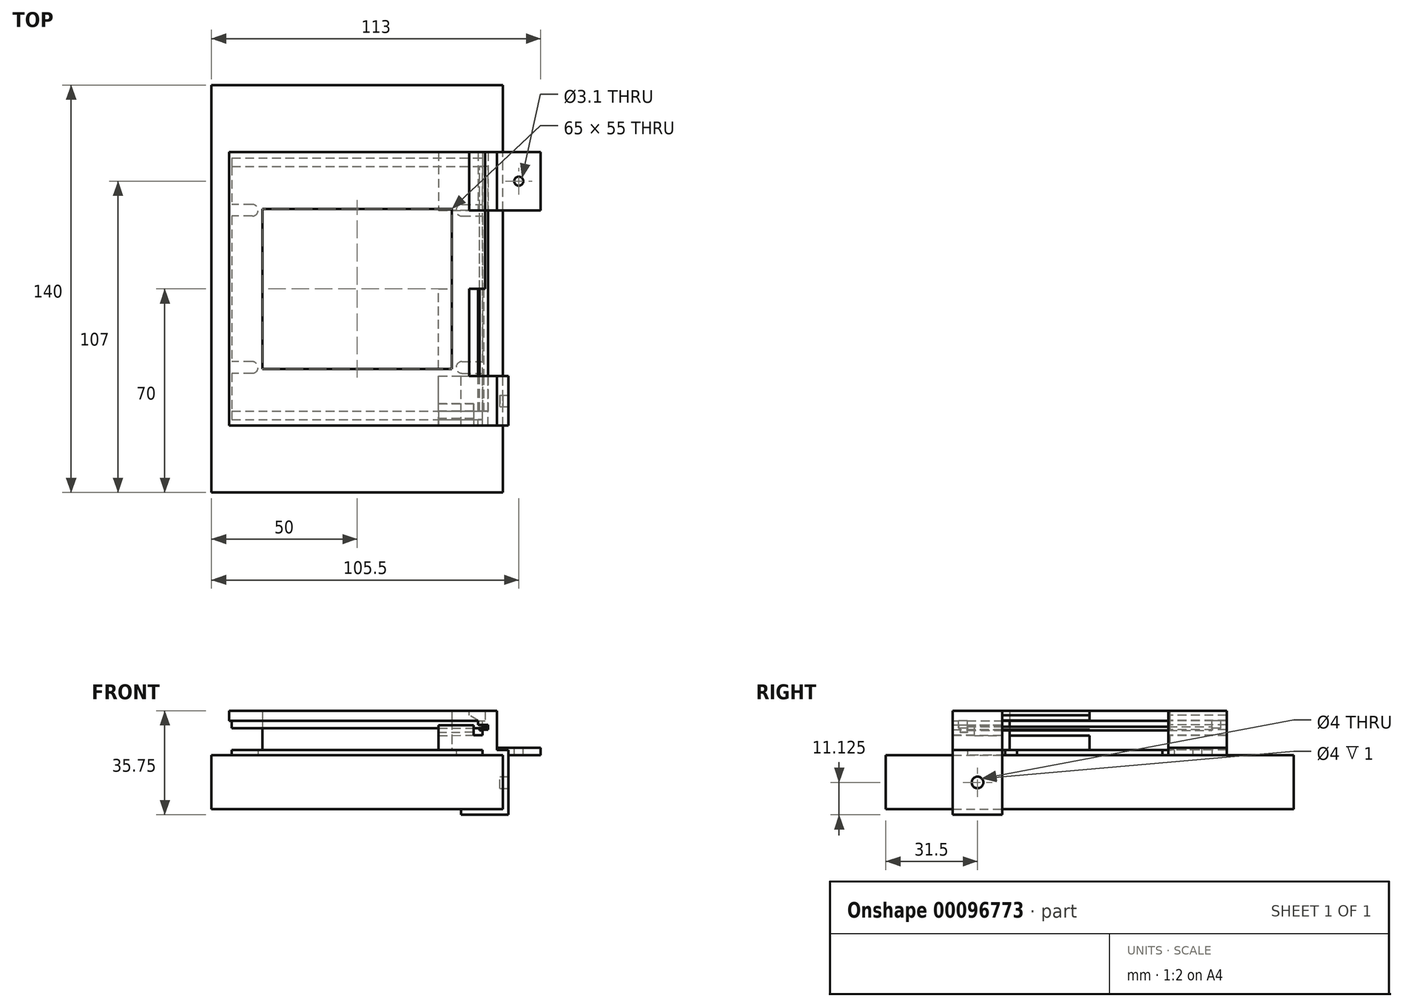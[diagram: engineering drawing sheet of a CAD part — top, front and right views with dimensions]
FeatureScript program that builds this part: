
annotation { "Feature Type Name" : "Feature", "Feature Type Description" : "" }
export const myFeature = defineFeature(function(context is Context, id is Id, definition is map)
    precondition{}
    {
        {
            var Q0;
            Q0=qCreatedBy(makeId("Top.planeOp"),FACE);
            var sketch = newSketch(context, id + "F0", { "sketchPlane" : qUnion([Q0])});
            skLineSegment(sketch, "E0.bottom", {"start": v(-50, -70) * mm, "end": v(50, -70) * mm});
            skLineSegment(sketch, "E0.top", {"start": v(-50, 70) * mm, "end": v(50, 70) * mm});
            skLineSegment(sketch, "E0.left", {"start": v(-50, -70) * mm, "end": v(-50, 70) * mm});
            skLineSegment(sketch, "E0.right", {"start": v(50, -70) * mm, "end": v(50, 70) * mm});
            skPoint(sketch, "E0.middle", {"position": v(0, 0) * mm});
            skSolve(sketch);
        }
        {
            var Q0;
            Q0=qSketchRegion(id+"F0",true);
            extrude(context, id + "F1", {"entities" : qUnion([Q0]), "oppositeDirection" : true, "depth" : 18.5 * mm});
        }
        {
            var Q0;
            Q0=qCreatedBy(makeId("Top.planeOp"),FACE);
            var sketch = newSketch(context, id + "F2", { "sketchPlane" : qUnion([Q0])});
            skLineSegment(sketch, "E1.bottom", {"start": v(-43, 42) * mm, "end": v(43, 42) * mm});
            skLineSegment(sketch, "E1.top", {"start": v(-43, -42) * mm, "end": v(43, -42) * mm});
            skLineSegment(sketch, "E1.left", {"start": v(-43, 42) * mm, "end": v(-43, 29) * mm});
            skLineSegment(sketch, "E1.right", {"start": v(43, 42) * mm, "end": v(43, 29) * mm});
            skPoint(sketch, "E1.middle", {"position": v(0, 0) * mm});
            skArc(sketch, "E2", {"start": v(-36, 25) * mm, "mid": v(-34, 27) * mm, "end": v(-36, 29) * mm});
            skLineSegment(sketch, "E3", {"start": v(-36, 25) * mm, "end": v(-43, 25) * mm});
            skLineSegment(sketch, "E4", {"start": v(-36, 29) * mm, "end": v(-43, 29) * mm});
            skArc(sketch, "E5.MirrorCS", {"start": v(36, 25) * mm, "mid": v(34, 27) * mm, "end": v(36, 29) * mm});
            skLineSegment(sketch, "E6.MirrorCS", {"start": v(36, 29) * mm, "end": v(43, 29) * mm});
            skLineSegment(sketch, "E7.MirrorCS", {"start": v(36, 25) * mm, "end": v(43, 25) * mm});
            skLineSegment(sketch, "E8.MirrorCS", {"start": v(-36, -25) * mm, "end": v(-43, -25) * mm});
            skLineSegment(sketch, "E9.MirrorCS", {"start": v(-36, -29) * mm, "end": v(-43, -29) * mm});
            skArc(sketch, "E10.MirrorCS", {"start": v(-36, -25) * mm, "mid": v(-34, -27) * mm, "end": v(-36, -29) * mm});
            skLineSegment(sketch, "E11.MirrorCS", {"start": v(36, -25) * mm, "end": v(43, -25) * mm});
            skLineSegment(sketch, "E12.MirrorCS", {"start": v(36, -29) * mm, "end": v(43, -29) * mm});
            skArc(sketch, "E13.MirrorCS", {"start": v(36, -25) * mm, "mid": v(34, -27) * mm, "end": v(36, -29) * mm});
            skLineSegment(sketch, "E14.trimOffspring", {"start": v(-43, 25) * mm, "end": v(-43, -25) * mm});
            skLineSegment(sketch, "E15.trimOffspring", {"start": v(-43, -29) * mm, "end": v(-43, -42) * mm});
            skLineSegment(sketch, "E16.trimOffspring", {"start": v(43, -29) * mm, "end": v(43, -42) * mm});
            skLineSegment(sketch, "E17.trimOffspring", {"start": v(43, 25) * mm, "end": v(43, -25) * mm});
            skSolve(sketch);
        }
        {
            var Q0;
            Q0=qSketchRegion(id+"F2",true);
            extrude(context, id + "F3", {"entities" : qUnion([Q0]), "depth" : 1.75 * mm});
        }
        {
            var Q0;
            Q0=makeQuery(id+"F3.opExtrude","CAP_FACE",FACE,{"disambiguationData":[OSD([sQuery(id+"F2.wireOp",EDGE,"E1.bottom"),sQuery(id+"F2.wireOp",EDGE,"E1.top"),sQuery(id+"F2.wireOp",EDGE,"E1.left"),sQuery(id+"F2.wireOp",EDGE,"E1.right"),sQuery(id+"F2.wireOp",EDGE,"E2"),sQuery(id+"F2.wireOp",EDGE,"E3"),sQuery(id+"F2.wireOp",EDGE,"E4"),sQuery(id+"F2.wireOp",EDGE,"E5.MirrorCS"),sQuery(id+"F2.wireOp",EDGE,"E6.MirrorCS"),sQuery(id+"F2.wireOp",EDGE,"E7.MirrorCS"),sQuery(id+"F2.wireOp",EDGE,"E8.MirrorCS"),sQuery(id+"F2.wireOp",EDGE,"E9.MirrorCS"),sQuery(id+"F2.wireOp",EDGE,"E10.MirrorCS"),sQuery(id+"F2.wireOp",EDGE,"E11.MirrorCS"),sQuery(id+"F2.wireOp",EDGE,"E12.MirrorCS"),sQuery(id+"F2.wireOp",EDGE,"E13.MirrorCS"),sQuery(id+"F2.wireOp",EDGE,"E14.trimOffspring"),sQuery(id+"F2.wireOp",EDGE,"E15.trimOffspring"),sQuery(id+"F2.wireOp",EDGE,"E16.trimOffspring"),sQuery(id+"F2.wireOp",EDGE,"E17.trimOffspring")])],"isStart":false});
            var sketch = newSketch(context, id + "F4", { "sketchPlane" : qUnion([Q0])});
            skLineSegment(sketch, "E18.bottom", {"start": v(-45, 47) * mm, "end": v(45, 47) * mm});
            skLineSegment(sketch, "E18.top", {"start": v(-45, -47) * mm, "end": v(45, -47) * mm});
            skLineSegment(sketch, "E18.left", {"start": v(-45, 47) * mm, "end": v(-45, -47) * mm});
            skLineSegment(sketch, "E18.right", {"start": v(45, 47) * mm, "end": v(45, -47) * mm});
            skPoint(sketch, "E18.middle", {"position": v(0, 0) * mm});
            skLineSegment(sketch, "E19.bottom", {"start": v(-43, 45) * mm, "end": v(43, 45) * mm});
            skLineSegment(sketch, "E19.top", {"start": v(-43, -45) * mm, "end": v(43, -45) * mm});
            skLineSegment(sketch, "E19.left", {"start": v(-43, 45) * mm, "end": v(-43, -45) * mm});
            skLineSegment(sketch, "E19.right", {"start": v(43, 45) * mm, "end": v(43, -45) * mm});
            skLineSegment(sketch, "E20", {"start": v(-43, 45) * mm, "end": v(-45, 45) * mm});
            skLineSegment(sketch, "E21", {"start": v(43, 45) * mm, "end": v(45, 45) * mm});
            skLineSegment(sketch, "E22.MirrorCS", {"start": v(-43, -45) * mm, "end": v(-45, -45) * mm});
            skLineSegment(sketch, "E23.MirrorCS", {"start": v(43, -45) * mm, "end": v(45, -45) * mm});
            skLineSegment(sketch, "E24", {"start": v(-43, 45) * mm, "end": v(-43, 47) * mm});
            skLineSegment(sketch, "E25.MirrorCS", {"start": v(43, 45) * mm, "end": v(43, 47) * mm});
            skLineSegment(sketch, "E26.MirrorCS", {"start": v(-43, -45) * mm, "end": v(-43, -47) * mm});
            skLineSegment(sketch, "E27.MirrorCS", {"start": v(43, -45) * mm, "end": v(43, -47) * mm});
            skLineSegment(sketch, "E28.bottom", {"start": v(-32.5, 27.5) * mm, "end": v(32.5, 27.5) * mm});
            skLineSegment(sketch, "E28.top", {"start": v(-32.5, -27.5) * mm, "end": v(32.5, -27.5) * mm});
            skLineSegment(sketch, "E28.left", {"start": v(-32.5, 27.5) * mm, "end": v(-32.5, -27.5) * mm});
            skLineSegment(sketch, "E28.right", {"start": v(32.5, 27.5) * mm, "end": v(32.5, -27.5) * mm});
            skSolve(sketch);
        }
        {
            var Q0;
            Q0=makeQuery(id+"F4.imprint","IMPRINT",FACE,{"disambiguationData":[TD([[makeQuery(id+"F4.imprint","IMPRINT",EDGE,{"derivedFrom":sQuery(id+"F4.wireOp",EDGE,"E28.bottom")}),-1.0]])]});
            extrude(context, id + "F5", {"entities" : qUnion([Q0]), "depth" : 10 * mm});
        }
        {
            var Q0;
            Q0=makeQuery(id+"F5.opExtrude","CAP_FACE",FACE,{"disambiguationData":[OSD([sQuery(id+"F4.wireOp",EDGE,"E28.bottom"),sQuery(id+"F4.wireOp",EDGE,"E28.top"),sQuery(id+"F4.wireOp",EDGE,"E28.left"),sQuery(id+"F4.wireOp",EDGE,"E28.right")])],"isStart":false});
            var sketch = newSketch(context, id + "F6", { "sketchPlane" : qUnion([Q0])});
            skLineSegment(sketch, "E29.bottom", {"start": v(-44, 47) * mm, "end": v(44, 47) * mm});
            skLineSegment(sketch, "E29.top", {"start": v(-44, -47) * mm, "end": v(44, -47) * mm});
            skLineSegment(sketch, "E29.left", {"start": v(-44, 47) * mm, "end": v(-44, -47) * mm});
            skLineSegment(sketch, "E29.right", {"start": v(44, 47) * mm, "end": v(44, -47) * mm});
            skPoint(sketch, "E29.middle", {"position": v(0, 0) * mm});
            skLineSegment(sketch, "E30.bottom", {"start": v(-43, 45) * mm, "end": v(43, 45) * mm});
            skLineSegment(sketch, "E30.top", {"start": v(-43, -45) * mm, "end": v(43, -45) * mm});
            skLineSegment(sketch, "E30.left", {"start": v(-43, 45) * mm, "end": v(-43, -45) * mm});
            skLineSegment(sketch, "E30.right", {"start": v(43, 45) * mm, "end": v(43, -45) * mm});
            skLineSegment(sketch, "E31.MirrorCS", {"start": v(-43, -44) * mm, "end": v(-43, -45) * mm});
            skLineSegment(sketch, "E32.MirrorCS", {"start": v(43, -44) * mm, "end": v(43, -45) * mm});
            skLineSegment(sketch, "E33.bottom", {"start": v(-32.5, 27.5) * mm, "end": v(32.5, 27.5) * mm});
            skLineSegment(sketch, "E33.top", {"start": v(-32.5, -27.5) * mm, "end": v(32.5, -27.5) * mm});
            skLineSegment(sketch, "E33.left", {"start": v(-32.5, 27.5) * mm, "end": v(-32.5, -27.5) * mm});
            skLineSegment(sketch, "E33.right", {"start": v(32.5, 27.5) * mm, "end": v(32.5, -27.5) * mm});
            skLineSegment(sketch, "E34.0", {"start": v(-43, 42) * mm, "end": v(43, 42) * mm});
            skLineSegment(sketch, "E35.0", {"start": v(-43, -42) * mm, "end": v(43, -42) * mm});
            skSolve(sketch);
        }
        {
            var Q0;
            Q0=makeQuery(id+"F6.imprint","IMPRINT",FACE,{"disambiguationData":[TD([[makeQuery(id+"F6.imprint","IMPRINT",EDGE,{"derivedFrom":sQuery(id+"F6.wireOp",EDGE,"E30.bottom")}),1.0]])]});
            var Q1;
            {var subQ0=sQuery(id+"F6.wireOp",EDGE,"E30.bottom");Q1=makeQuery(id+"F6.imprint","IMPRINT",FACE,{"disambiguationData":[TD([[makeQuery(id+"F6.imprint","IMPRINT",EDGE,{"derivedFrom":subQ0}),-1.0]])]});}
            var Q2;
            Q2=makeQuery(id+"F6.imprint","IMPRINT",FACE,{"disambiguationData":[TD([[makeQuery(id+"F6.imprint","IMPRINT",EDGE,{"derivedFrom":sQuery(id+"F6.wireOp",EDGE,"E33.bottom")}),1.0]])]});
            var Q3;
            {var subQ0=sQuery(id+"F6.wireOp",EDGE,"E30.top");Q3=makeQuery(id+"F6.imprint","IMPRINT",FACE,{"disambiguationData":[TD([[makeQuery(id+"F6.imprint","IMPRINT",EDGE,{"derivedFrom":subQ0}),1.0]])]});}
            var Q4;
            Q4=makeQuery(id+"F6.imprint","IMPRINT",FACE,{"disambiguationData":[TD([[makeQuery(id+"F6.imprint","IMPRINT",EDGE,{"derivedFrom":sQuery(id+"F6.wireOp",EDGE,"E30.top")}),-1.0]])]});
            extrude(context, id + "F7", {"entities" : qUnion([Q0, Q1, Q2, Q3, Q4]), "depth" : 3.5 * mm});
        }
        {
            var Q0;
            {var subQ0=sQuery(id+"F6.wireOp",EDGE,"E30.bottom");Q0=makeQuery(id+"F6.imprint","IMPRINT",FACE,{"disambiguationData":[TD([[makeQuery(id+"F6.imprint","IMPRINT",EDGE,{"derivedFrom":subQ0}),-1.0]])]});}
            var Q1;
            {var subQ0=sQuery(id+"F6.wireOp",EDGE,"E30.top");Q1=makeQuery(id+"F6.imprint","IMPRINT",FACE,{"disambiguationData":[TD([[makeQuery(id+"F6.imprint","IMPRINT",EDGE,{"derivedFrom":subQ0}),1.0]])]});}
            extrude(context, id + "F8", {"entities" : qUnion([Q0, Q1]), "operationType" : NewBodyOperationType.ADD, "oppositeDirection" : true, "depth" : 2.5 * mm});
        }
        {
            var Q0;
            Q0=qCreatedBy(makeId("Front.planeOp"),FACE);
            var sketch = newSketch(context, id + "F9", { "sketchPlane" : qUnion([Q0])});
            skLineSegment(sketch, "E36.0", {"start": v(43, 13.75) * mm, "end": v(43, 10.25) * mm});
            skLineSegment(sketch, "E37.0", {"start": v(43, 13.75) * mm, "end": v(43, 9.75) * mm});
            skLineSegment(sketch, "E38.0", {"start": v(43, 7.25) * mm, "end": v(43, 9.75) * mm});
            skLineSegment(sketch, "E39", {"start": v(43, 9.75) * mm, "end": v(43, 8.5) * mm});
            skLineSegment(sketch, "E40", {"start": v(43, 8.5) * mm, "end": v(45, 9.75) * mm});
            skLineSegment(sketch, "E41", {"start": v(45, 9.75) * mm, "end": v(43, 9.75) * mm});
            skLineSegment(sketch, "E42.bottom", {"start": v(43, 9.75) * mm, "end": v(42, 9.75) * mm});
            skLineSegment(sketch, "E42.top", {"start": v(43, 8.5) * mm, "end": v(42, 8.5) * mm});
            skLineSegment(sketch, "E42.right", {"start": v(42, 9.75) * mm, "end": v(42, 8.5) * mm});
            skSolve(sketch);
        }
        {
            var Q0;
            Q0=qSketchRegion(id+"F9",true);
            extrude(context, id + "F10", {"entities" : qUnion([Q0]), "operationType" : NewBodyOperationType.ADD, "depth" : 42 * mm, "hasSecondDirection" : true, "secondDirectionOppositeDirection" : true, "secondDirectionDepth" : 42 * mm});
        }
        {
            var Q0;
            Q0=qCreatedBy(makeId("Front.planeOp"),FACE);
            var sketch = newSketch(context, id + "F11", { "sketchPlane" : qUnion([Q0])});
            skLineSegment(sketch, "E43.0", {"start": v(28, 1.75) * mm, "end": v(43, 1.75) * mm});
            skLineSegment(sketch, "E44.0", {"start": v(43, 1.75) * mm, "end": v(43, 0) * mm});
            skLineSegment(sketch, "E45", {"start": v(43, 0) * mm, "end": v(48, 0) * mm});
            skPoint(sketch, "E46.orphan", {"position": v(43, 9.75) * mm});
            skPoint(sketch, "E47.orphan", {"position": v(-43, 9.25) * mm});
            skPoint(sketch, "E48.orphan", {"position": v(-43, 1.75) * mm});
            skPoint(sketch, "E49.end.orphan", {"position": v(43, 7.25) * mm});
            skLineSegment(sketch, "E50", {"start": v(27.97, 6.75) * mm, "end": v(28, 1.75) * mm});
            skLineSegment(sketch, "E51", {"start": v(48, 13.75) * mm, "end": v(48, 1.75) * mm});
            skPoint(sketch, "E52.0.end.orphan", {"position": v(45, 9.75) * mm});
            skLineSegment(sketch, "E53.0", {"start": v(45, 9.75) * mm, "end": v(43, 9.75) * mm, "construction": true});
            skLineSegment(sketch, "E54.0", {"start": v(43, 8.5) * mm, "end": v(45, 9.75) * mm, "construction": true});
            skLineSegment(sketch, "E55", {"start": v(27.97, 6.75) * mm, "end": v(43, 6.84) * mm});
            skLineSegment(sketch, "E56.bottom", {"start": v(43, 0) * mm, "end": v(52, 0) * mm});
            skLineSegment(sketch, "E56.top", {"start": v(48, 1.75) * mm, "end": v(52, 1.75) * mm});
            skLineSegment(sketch, "E56.left", {"start": v(43, 0) * mm, "end": v(43, 1.75) * mm});
            skLineSegment(sketch, "E57.right", {"start": v(41.5, 11.88) * mm, "end": v(41.5, 10.45) * mm});
            skLineSegment(sketch, "E58", {"start": v(38.5, 13.75) * mm, "end": v(41.5, 11.88) * mm});
            skLineSegment(sketch, "E59", {"start": v(41.5, 10.45) * mm, "end": v(44.97, 10.45) * mm});
            skLineSegment(sketch, "E60", {"start": v(44.97, 10.45) * mm, "end": v(45, 8.79) * mm});
            skLineSegment(sketch, "E61", {"start": v(45, 8.79) * mm, "end": v(43, 8.75) * mm});
            skPoint(sketch, "E62.orphan", {"position": v(43, 10) * mm});
            skPoint(sketch, "E63.orphan", {"position": v(41.5, 10) * mm});
            skLineSegment(sketch, "E64", {"start": v(43, 8.75) * mm, "end": v(43, 6.84) * mm});
            skLineSegment(sketch, "E65.top", {"start": v(38.5, 15.25) * mm, "end": v(48, 15.25) * mm});
            skLineSegment(sketch, "E65.left", {"start": v(38.5, 13.75) * mm, "end": v(38.5, 15.25) * mm});
            skLineSegment(sketch, "E65.right", {"start": v(48, 13.75) * mm, "end": v(48, 15.25) * mm});
            skPoint(sketch, "E57.bottom.end.orphan", {"position": v(41.5, 13.75) * mm});
            skLineSegment(sketch, "E66.0", {"start": v(50, -18.5) * mm, "end": v(50, 0) * mm});
            skLineSegment(sketch, "E67.0", {"start": v(-50, -18.5) * mm, "end": v(50, -18.5) * mm});
            skLineSegment(sketch, "E68", {"start": v(48, 0) * mm, "end": v(50, 0) * mm});
            skLineSegment(sketch, "E69", {"start": v(50, -18.5) * mm, "end": v(35.7, -18.5) * mm});
            skLineSegment(sketch, "E70", {"start": v(35.7, -18.5) * mm, "end": v(35.7, -20.5) * mm});
            skLineSegment(sketch, "E71", {"start": v(35.7, -20.5) * mm, "end": v(52, -20.5) * mm});
            skLineSegment(sketch, "E72", {"start": v(52, -20.5) * mm, "end": v(52, 1.75) * mm});
            skPoint(sketch, "E56.right.end.orphan", {"position": v(63, 1.75) * mm});
            skSolve(sketch);
        }
        {
            var Q0;
            Q0=qSketchRegion(id+"F11",true);
            extrude(context, id + "F12", {"entities" : qUnion([Q0]), "depth" : 47 * mm});
        }
        {
            var Q0;
            Q0=qSketchRegion(id+"F11",true);
            extrude(context, id + "F13", {"entities" : qUnion([Q0]), "operationType" : NewBodyOperationType.REMOVE, "depth" : 30 * mm});
        }
        {
            var Q0;
            Q0=makeQuery(id+"F12.opExtrude","SWEPT_FACE",FACE,{"disambiguationData":[OSD([sQuery(id+"F11.wireOp",EDGE,"E50")])]});
            var sketch = newSketch(context, id + "F14", { "sketchPlane" : qUnion([Q0])});
            skPoint(sketch, "E73.right.end.orphan", {"position": v(-45, -81.5) * mm});
            skPoint(sketch, "E74.0.end.orphan", {"position": v(42, 12) * mm});
            skPoint(sketch, "E74.0.start.orphan", {"position": v(-42, 9.5) * mm});
            skPoint(sketch, "E75.0.end.orphan", {"position": v(-45, 12) * mm});
            skPoint(sketch, "E75.0.start.orphan", {"position": v(-45, 9.5) * mm});
            skPoint(sketch, "E76.0.end.orphan", {"position": v(-45, 9.08) * mm});
            skPoint(sketch, "E76.0.start.orphan", {"position": v(42, 7.08) * mm});
            skPoint(sketch, "E77.0.3.end.orphan", {"position": v(47, 6.58) * mm});
            skPoint(sketch, "E77.0.3.start.orphan", {"position": v(47, 6.58) * mm});
            skPoint(sketch, "E77.0.1.end.orphan", {"position": v(30, 6.58) * mm});
            skPoint(sketch, "E77.0.1.start.orphan", {"position": v(30, 6.58) * mm});
            skLineSegment(sketch, "E78.0", {"start": v(-45, 9.5) * mm, "end": v(-45, 12) * mm, "construction": true});
            skLineSegment(sketch, "E79.0", {"start": v(42, 8.25) * mm, "end": v(42, 9.58) * mm, "construction": true});
            skLineSegment(sketch, "E80.0", {"start": v(-45, 12) * mm, "end": v(-46, 12) * mm, "construction": true});
            skLineSegment(sketch, "E81.0", {"start": v(-45, 12) * mm, "end": v(-135, 12) * mm, "construction": true});
            skLineSegment(sketch, "E82.top", {"start": v(47, 5.94) * mm, "end": v(39.5, 5.94) * mm});
            skPoint(sketch, "E83.orphan", {"position": v(39.5, 7.08) * mm});
            skLineSegment(sketch, "E84", {"start": v(-45, 11.58) * mm, "end": v(-45, 9.08) * mm});
            skLineSegment(sketch, "E85", {"start": v(47, 10.08) * mm, "end": v(47, 5.94) * mm});
            skPoint(sketch, "E86.orphan", {"position": v(-42, 8.25) * mm});
            skLineSegment(sketch, "E87.right", {"start": v(47, 10.08) * mm, "end": v(47, 7.08) * mm});
            skPoint(sketch, "E88.orphan", {"position": v(45, 12) * mm});
            skPoint(sketch, "E89.0.start.orphan", {"position": v(45, 9.5) * mm});
            skLineSegment(sketch, "E90", {"start": v(44.5, 10.08) * mm, "end": v(44.5, 7.58) * mm});
            skLineSegment(sketch, "E91", {"start": v(42, 7.58) * mm, "end": v(42, 9.58) * mm});
            skLineSegment(sketch, "E92", {"start": v(39.5, 9.58) * mm, "end": v(39.5, 5.94) * mm});
            skLineSegment(sketch, "E93", {"start": v(42, 7.58) * mm, "end": v(44.5, 7.58) * mm});
            skLineSegment(sketch, "E94.top", {"start": v(42, 10.08) * mm, "end": v(39.5, 10.08) * mm});
            skLineSegment(sketch, "E94.left", {"start": v(42, 9.58) * mm, "end": v(42, 10.08) * mm});
            skLineSegment(sketch, "E94.right", {"start": v(39.5, 9.58) * mm, "end": v(39.5, 10.08) * mm});
            skLineSegment(sketch, "E95", {"start": v(44.5, 10.08) * mm, "end": v(47, 10.08) * mm});
            skSolve(sketch);
        }
        {
            var Q0;
            Q0=qSketchRegion(id+"F14",true);
            extrude(context, id + "F15", {"entities" : qUnion([Q0]), "operationType" : NewBodyOperationType.ADD, "oppositeDirection" : true, "depth" : 12 * mm});
        }
        {
            var Q0;
            Q0=makeQuery(id+"F12.opExtrude","SWEPT_FACE",FACE,{"disambiguationData":[OSD([sQuery(id+"F11.wireOp",EDGE,"E72")])]});
            var sketch = newSketch(context, id + "F16", { "sketchPlane" : qUnion([Q0])});
            skCircle(sketch, "E96", {"center": v(-38.5, -9.38) * mm, "radius": 2 * mm});
            skPoint(sketch, "E96.centerSnap0", {"position": v(-47, -9.38) * mm});
            skPoint(sketch, "E96.centerSnap1", {"position": v(-38.5, 1.75) * mm});
            skSolve(sketch);
        }
        {
            var Q0;
            Q0=qSketchRegion(id+"F16",true);
            extrude(context, id + "F17", {"entities" : qUnion([Q0]), "operationType" : NewBodyOperationType.REMOVE, "oppositeDirection" : true, "depth" : 3 * mm});
        }
        {
            var Q0;
            Q0=makeQuery(id+"F13.boolean.opBoolean","COPY",FACE,{"derivedFrom":makeQuery(id+"F13.opExtrude","CAP_FACE",FACE,{"disambiguationData":[OSD([sQuery(id+"F11.wireOp",EDGE,"E43.0"),sQuery(id+"F11.wireOp",EDGE,"E50"),sQuery(id+"F11.wireOp",EDGE,"E51"),sQuery(id+"F11.wireOp",EDGE,"E55"),sQuery(id+"F11.wireOp",EDGE,"E56.bottom"),sQuery(id+"F11.wireOp",EDGE,"E56.top"),sQuery(id+"F11.wireOp",EDGE,"E56.left"),sQuery(id+"F11.wireOp",EDGE,"E57.right"),sQuery(id+"F11.wireOp",EDGE,"E58"),sQuery(id+"F11.wireOp",EDGE,"E59"),sQuery(id+"F11.wireOp",EDGE,"E60"),sQuery(id+"F11.wireOp",EDGE,"E61"),sQuery(id+"F11.wireOp",EDGE,"E64"),sQuery(id+"F11.wireOp",EDGE,"E65.top"),sQuery(id+"F11.wireOp",EDGE,"E65.left"),sQuery(id+"F11.wireOp",EDGE,"E65.right"),sQuery(id+"F11.wireOp",EDGE,"E66.0"),sQuery(id+"F11.wireOp",EDGE,"E68"),sQuery(id+"F11.wireOp",EDGE,"E69"),sQuery(id+"F11.wireOp",EDGE,"E70"),sQuery(id+"F11.wireOp",EDGE,"E71"),sQuery(id+"F11.wireOp",EDGE,"E72")])],"isStart":false})});
            cPlane(context, id + "F18", {"entities" : qUnion([Q0]), "cplaneType" : CPlaneType.OFFSET, "offset" : 57 * mm, "width" : 150 * mm, "height" : 150 * mm});
        }
        {
            var Q0;
            Q0=qCreatedBy(id+"F18.planeOp",FACE);
            var sketch = newSketch(context, id + "F19", { "sketchPlane" : qUnion([Q0])});
            skLineSegment(sketch, "E97.0.0", {"start": v(-28, 1.75) * mm, "end": v(-27.97, 6.75) * mm});
            skLineSegment(sketch, "E97.0.1", {"start": v(-27.97, 6.75) * mm, "end": v(-43, 6.84) * mm});
            skLineSegment(sketch, "E97.0.2", {"start": v(-43, 6.84) * mm, "end": v(-43, 8.75) * mm});
            skLineSegment(sketch, "E97.0.3", {"start": v(-43, 8.75) * mm, "end": v(-45, 8.79) * mm});
            skLineSegment(sketch, "E97.0.4", {"start": v(-45, 8.79) * mm, "end": v(-44.97, 10.45) * mm});
            skLineSegment(sketch, "E97.0.5", {"start": v(-44.97, 10.45) * mm, "end": v(-41.5, 10.45) * mm});
            skLineSegment(sketch, "E97.0.6", {"start": v(-41.5, 10.45) * mm, "end": v(-41.5, 11.88) * mm});
            skLineSegment(sketch, "E97.0.7", {"start": v(-41.5, 11.88) * mm, "end": v(-38.5, 13.75) * mm});
            skLineSegment(sketch, "E97.0.8", {"start": v(-38.5, 13.75) * mm, "end": v(-38.5, 15.25) * mm});
            skLineSegment(sketch, "E97.0.9", {"start": v(-38.5, 15.25) * mm, "end": v(-48, 15.25) * mm});
            skLineSegment(sketch, "E97.0.10", {"start": v(-48, 15.25) * mm, "end": v(-48, 2.5) * mm});
            skLineSegment(sketch, "E97.0.18", {"start": v(-43, 0) * mm, "end": v(-43, 1.75) * mm});
            skLineSegment(sketch, "E97.0.19", {"start": v(-43, 1.75) * mm, "end": v(-28, 1.75) * mm});
            skPoint(sketch, "E97.0.16.end.orphan", {"position": v(-50, 0) * mm});
            skPoint(sketch, "E97.0.15.end.orphan", {"position": v(-50, -18.5) * mm});
            skPoint(sketch, "E97.0.13.start.orphan", {"position": v(-52, -20.5) * mm});
            skPoint(sketch, "E97.0.14.end.orphan", {"position": v(-35.7, -18.5) * mm});
            skPoint(sketch, "E97.0.14.start.orphan", {"position": v(-35.7, -20.5) * mm});
            skLineSegment(sketch, "E98.bottom", {"start": v(-43, 0) * mm, "end": v(-63, 0) * mm});
            skLineSegment(sketch, "E98.top", {"start": v(-48, 2.5) * mm, "end": v(-63, 2.5) * mm});
            skLineSegment(sketch, "E98.right", {"start": v(-63, 0) * mm, "end": v(-63, 2.5) * mm});
            skPoint(sketch, "E97.0.11.end.orphan", {"position": v(-52, 1.75) * mm});
            skPoint(sketch, "E99.orphan", {"position": v(-48, 1.75) * mm});
            skLineSegment(sketch, "E100.0", {"start": v(-39.97, 6.82) * mm, "end": v(-39.95, 10.32) * mm, "construction": true});
            skSolve(sketch);
        }
        {
            var Q0;
            Q0 = qSketchRegion(id + "F19", true);
            extrude(context, id + "F20", {"entities" : qUnion([Q0]), "depth" : 20 * mm});
        }
        {
            var Q0;
            Q0=makeQuery(id+"F20.opExtrude","SWEPT_FACE",FACE,{"disambiguationData":[OSD([sQuery(id+"F19.wireOp",EDGE,"E98.top")])]});
            var sketch = newSketch(context, id + "F21", { "sketchPlane" : qUnion([Q0])});
            skLineSegment(sketch, "E101.0.0", {"start": v(48, 27) * mm, "end": v(63, 27) * mm, "construction": true});
            skLineSegment(sketch, "E101.0.1", {"start": v(63, 27) * mm, "end": v(63, 47) * mm, "construction": true});
            skLineSegment(sketch, "E101.0.2", {"start": v(63, 47) * mm, "end": v(48, 47) * mm, "construction": true});
            skLineSegment(sketch, "E101.0.3", {"start": v(48, 47) * mm, "end": v(48, 27) * mm, "construction": true});
            skPoint(sketch, "E102", {"position": v(55.5, 37) * mm});
            skPoint(sketch, "E102.positionSnap0", {"position": v(63, 37) * mm});
            skPoint(sketch, "E102.positionSnap1", {"position": v(55.5, 27) * mm});
            skCircle(sketch, "E103", {"center": v(55.5, 37) * mm, "radius": 1.55 * mm});
            skSolve(sketch);
        }
        {
            var Q0;
            Q0 = qSketchRegion(id + "F21", true);
            extrude(context, id + "F22", {"entities" : qUnion([Q0]), "operationType" : NewBodyOperationType.REMOVE, "oppositeDirection" : true, "depth" : 25 * mm});
        }
    });
